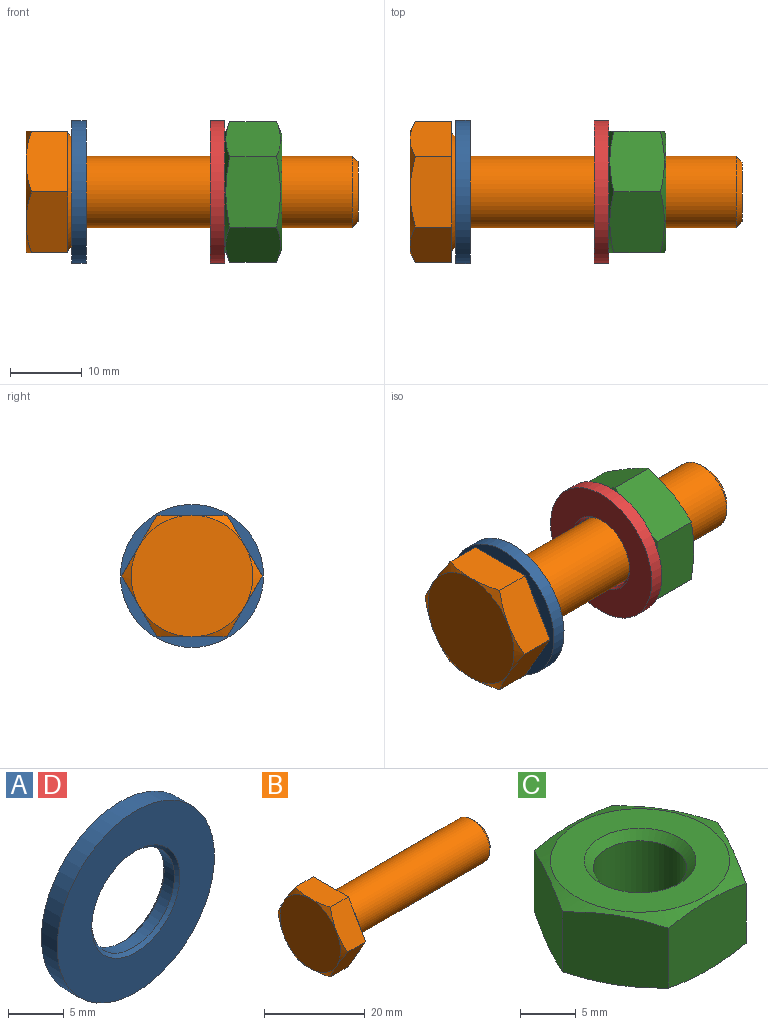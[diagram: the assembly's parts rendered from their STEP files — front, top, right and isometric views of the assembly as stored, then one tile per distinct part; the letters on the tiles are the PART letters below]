
ASSEMBLY  parts=4 mates=5
PART A: 6 faces, bbox 20x2x20 mm
  f0: cone r=5.42mm half-angle=45deg, axis (0,-1,0), area 16.9mm2, adj f1,f5
  f1: cylinder r=5.25mm len=10.5mm, axis (0,1,0), area 42.9mm2, adj f0,f2
  f2: cone r=5.42mm half-angle=45deg, axis (0,1,0), area 16.9mm2, adj f1,f4
  f3: cylinder r=10mm len=20mm, axis (0,1,0), area 125.7mm2, adj f4,f5
  f4: plane 20x20mm, normal (0,1,0), area 215.6mm2, adj f2,f3
  f5: plane 20x20mm, normal (0,-1,0), area 215.6mm2, adj f0,f3
PART B: 24 faces, bbox 46.4x19.6x19.6 mm
  f0: cone r=9.16mm half-angle=60deg, axis (1,0,0), area 4.5mm2, adj f19,f21,f22
  f1: cone r=9.16mm half-angle=60deg, axis (1,0,0), area 4.5mm2, adj f16,f17,f22
  f2: cone r=4.59mm half-angle=45deg, axis (-1,0,0), area 33.1mm2, adj f3,f11
  f3: cylinder r=5mm len=37.69mm, axis (1,0,0), area 1184mm2, adj f2,f10
  f4: cone r=4.59mm half-angle=45deg, axis (-1,0,0), area 33.1mm2, adj f5,f10
  f5: cylinder r=5mm len=10mm, axis (1,0,0), area 9.1mm2, adj f4,f6
  f6: torus R=5.4mm, axis (1,0,0), area 20.3mm2, adj f5,f9
  f7: cylinder r=7.8mm len=15.6mm, axis (1,0,0), area 4.9mm2, adj f8,f9
  f8: cone r=8.05mm half-angle=45deg, axis (-1,0,0), area 35.8mm2, adj f7,f23
  f9: plane 15.6x15.6mm, normal (1,0,0), area 99.5mm2, adj f6,f7
  f10: plane 10x10mm, normal (-1,0,0), area 23.4mm2, adj f3,f4
  f11: plane 8.38x8.38mm, normal (1,0,0), area 55.1mm2, adj f2
  f12: cone r=9.16mm half-angle=60deg, axis (1,0,0), area 4.5mm2, adj f17,f18,f22
  f13: cone r=9.16mm half-angle=60deg, axis (1,0,0), area 4.5mm2, adj f16,f20,f22
  f14: cone r=9.16mm half-angle=60deg, axis (1,0,0), area 4.5mm2, adj f19,f20,f22
  f15: cone r=9.16mm half-angle=60deg, axis (1,0,0), area 4.5mm2, adj f18,f21,f22
  f16: plane 8.51x5.8mm, normal (0,-0.87,0.5), area 54.4mm2, adj f1,f13,f17,f20,f23
  f17: plane 8.51x5.8mm, normal (0,-0.87,-0.5), area 54.4mm2, adj f1,f12,f16,f18,f23
  f18: plane 9.83x5.8mm, normal (0,0,-1), area 54.4mm2, adj f12,f15,f17,f21,f23
  f19: plane 8.51x5.8mm, normal (0,0.87,0.5), area 54.4mm2, adj f0,f14,f20,f21,f23
  f20: plane 9.83x5.8mm, normal (0,0,1), area 54.4mm2, adj f13,f14,f16,f19,f23
  f21: plane 8.51x5.8mm, normal (0,0.87,-0.5), area 54.4mm2, adj f0,f15,f18,f19,f23
  f22: plane 17x17mm, normal (-1,0,0), area 227mm2, adj f0,f1,f12,f13,f14,f15
  f23: plane 19.63x17mm, normal (1,0,0), area 33.9mm2, adj f8,f16,f17,f18,f19,f20,f21
PART C: 13 faces, bbox 19.6x19.6x8.2 mm
  f0: cone r=4.59mm half-angle=45deg, axis (0,0,-1), area 33.1mm2, adj f1,f10
  f1: cylinder r=4.19mm len=8.38mm, axis (0,0,1), area 167.8mm2, adj f0,f2
  f2: cone r=4.59mm half-angle=45deg, axis (0,0,1), area 33.1mm2, adj f1,f9
  f3: cone r=8.91mm half-angle=68deg, axis (0,0,-1), area 52.3mm2, adj f5,f6,f7,f8,f9,f11,f12
  f4: cone r=8.91mm half-angle=68deg, axis (0,0,1), area 52.3mm2, adj f5,f6,f7,f8,f10,f11,f12
  f5: plane 8.5x8.19mm, normal (-0.87,0.5,0), area 71.1mm2, adj f3,f4,f6,f12
  f6: plane 9.82x8.19mm, normal (0,1,0), area 71.1mm2, adj f3,f4,f5,f7
  f7: plane 8.5x8.19mm, normal (0.87,0.5,0), area 71.1mm2, adj f3,f4,f6,f8
  f8: plane 8.5x8.19mm, normal (0.87,-0.5,0), area 71.1mm2, adj f3,f4,f7,f11
  f9: plane 16.03x16.03mm, normal (0,0,1), area 123.3mm2, adj f2,f3
  f10: plane 16.03x16.03mm, normal (0,0,-1), area 123.3mm2, adj f0,f4
  f11: plane 9.82x8.19mm, normal (0,-1,0), area 71.1mm2, adj f3,f4,f8,f12
  f12: plane 8.5x8.19mm, normal (-0.87,-0.5,0), area 71.1mm2, adj f3,f4,f5,f11
PART D: same geometry as A
PLACE A rot(axis=(0.58,0.58,-0.58),120deg) t=(-50.48,35.69,-41.69)mm
PLACE B t=(-51.08,35.69,-41.69)mm
PLACE C rot(axis=(0,1,0),90deg) t=(-29.14,35.69,-41.69)mm
PLACE D rot(axis=(0.58,0.58,-0.58),120deg) t=(-31.14,35.69,-41.69)mm
MATE planar C.f0 <-> D.f0  axis (-1,0,0) through (-29.14,35.69,-41.69)mm
MATE planar A.f0 <-> B.f2  axis (-1,0,0) through (-50.48,35.69,-41.69)mm
MATE cylindrical C.f0 <-> B.f2  axis (1,0,0) through (-28.32,35.69,-41.69)mm
MATE cylindrical A.f0 <-> B.f2  axis (1,0,0) through (-49.48,35.69,-41.69)mm
MATE cylindrical D.f0 <-> B.f2  axis (1,0,0) through (-30.14,35.69,-41.69)mm
